# Revit family: Hager-Univers-IP31-syst-Aufputz-NoHosted-DE-de
name_source: partatom
category: Electrical Equipment
units: mm (PartAtom-declared; Revit-internal decimal feet)

## family parameters
Always vertical = Yes
Cut with Voids When Loaded = No
Panel Configuration = Two Columns, Circuits Across
Part Type = Panelboard
Room Calculation Point = No
Round Connector Dimension = Use Diameter
Shared = No
Work Plane-Based = Yes

## types (8) — shared parameters
Default Elevation = 1219 mm
EF000007 - Farbe = EV000202 - weiß
EF000049 - Tiefe = 161 mm  [stored 0.528215 ft]
EF000116 - RAL-Nummer = 9010
EF000339 - Art der Abdeckung = EV004216 - Tür
EF001062 - EMV-Ausführung = No
EF001088 - Anbaumöglichkeit = Yes
EF001131 - Innentiefe = 160 mm
EF001134 - DIN-Schiene = Yes
EF002950 - Breite in Teilungseinheiten = 12
EF005474 - Schutzart (IP) = EV006411 - IP31
EF006244 - Transparenter Deckel/Tür = No
EF006306 - Mit Schloss = No
EF015941 - Signaldurchlassende Tür = No
HG000002 - Mit tür = Yes
HG000003 - Bereich = Univers
HG000005 - Dicke = 3 mm  [stored 0.00984252 ft]
HG000006 - Unterputz = No
HG000007 - Anzahl der leeren Spalten = 1
HG000011 - Leere Reihen von unten = No
HG000017 - Distanz zwischen den Polen = 18 mm  [stored 0.0590551 ft]
Manufacturer = Hager
Type Comments = Univers

## per-type parameters (varying)
| type | EF000003 - Montageart | EF000008 - Breite | EF000040 - Höhe | EF000118 - Mit Montageplatte | EF000218 - Einbautiefe | EF000266 - Anzahl der Reihen | EF000332 - Einbauhöhe | EF000846 - Einbaubreite | EF001596 - Werkstoff des Gehäuses | EF004462 - Art der Schließung | EF009212 - Ausführung Deckel | EF015776 - Erdungsklemmenblock | EF015777 - Neutralleiterklemmenblock | HG000001 - Anzahl der Spalten | HG000004 - Herstellerreferenz | HG000008 - Anzahl der leeren Reihen | HG000009 - Doppelflügeligen Tür | HG000010 - Asymmetrische Türen | Model |
| Aufputz IP31 B550 H1100 T161 12 Teilungseinheiten - FWB72K1 | EV001247 - Aufputz/Unterputz | 550 mm | 1100 mm | Yes | 161 mm  [stored 0.528215 ft] | 7 | 1100 mm | 550 mm |  |  | EV000116 - geschlossen | No | No | 1 | FWB72K1 | 7 | No | No | FWB72K1 |
| Aufputz IP31 B550 H500 T161 12 Teilungseinheiten - FWB32K1 | EV000384 - Aufputz | 550 mm | 500 mm  [stored 1.64042 ft] | Yes | 0 mm  [stored 0 ft] | 3 | 0 mm  [stored 0 ft] | 0 mm  [stored 0 ft] | EV000179 - Stahl | EV000154 - sonstige | EV000116 - geschlossen | No | No | 1 | FWB32K1 | 3 | No | No | FWB32K1 |
| Aufputz IP31 B550 H650 T161 12 Teilungseinheiten - FWB42K1 | EV000384 - Aufputz | 550 mm | 650 mm | Yes | 0 mm  [stored 0 ft] | 4 | 0 mm  [stored 0 ft] | 0 mm  [stored 0 ft] |  |  |  | No | No | 1 | FWB42K1 | 4 | No | No | FWB42K1 |
| Aufputz IP31 B550 H650 T161 12 Teilungseinheiten - FWB42K4 | EV000384 - Aufputz | 550 mm | 650 mm | Yes | 0 mm  [stored 0 ft] | 4 | 0 mm  [stored 0 ft] | 0 mm  [stored 0 ft] | EV000179 - Stahl | EV000154 - sonstige | EV000116 - geschlossen | No | Yes | 1 | FWB42K4 | 4 | No | No | FWB42K4 |
| Aufputz IP31 B550 H800 T161 12 Teilungseinheiten - FWB52K1 | EV001247 - Aufputz/Unterputz | 550 mm | 800 mm  [stored 2.62467 ft] | Yes | 161 mm  [stored 0.528215 ft] | 5 | 800 mm  [stored 2.62467 ft] | 550 mm |  |  | EV000116 - geschlossen | Yes | Yes | 1 | FWB52K1 | 5 | No | No | FWB52K1 |
| Aufputz IP31 B550 H800 T161 12 Teilungseinheiten - FWB52K4 | EV000384 - Aufputz | 550 mm | 800 mm  [stored 2.62467 ft] | Yes | 0 mm  [stored 0 ft] | 5 | 0 mm  [stored 0 ft] | 0 mm  [stored 0 ft] | EV000179 - Stahl | EV000154 - sonstige | EV000116 - geschlossen | No | Yes | 1 | FWB52K4 | 5 | No | No | FWB52K4 |
| Aufputz IP31 B550 H950 T161 12 Teilungseinheiten - FWB62K1 | EV001247 - Aufputz/Unterputz | 550 mm | 950 mm  [stored 3.1168 ft] | Yes | 161 mm  [stored 0.528215 ft] | 6 | 950 mm  [stored 3.1168 ft] | 550 mm |  |  | EV000116 - geschlossen | No | No | 1 | FWB62K1 | 6 | No | No | FWB62K1 |
| Aufputz IP31 B800 H800 T161 12 Teilungseinheiten - FWB53K1 | EV001247 - Aufputz/Unterputz | 800 mm  [stored 2.62467 ft] | 800 mm  [stored 2.62467 ft] | No | 161 mm  [stored 0.528215 ft] | 10 | 800 mm  [stored 2.62467 ft] | 800 mm  [stored 2.62467 ft] |  | EV000154 - sonstige | EV000116 - geschlossen | No | No | 2 | FWB53K1 | 5 | Yes | Yes | FWB53K1 |

note: [stored X ft] marks values corroborated as IEEE doubles in the binary element streams (Revit-internal decimal feet)

## geometry (parser evidence)
native form markers: Sweep x13
no freeform markers — native parametric forms only
